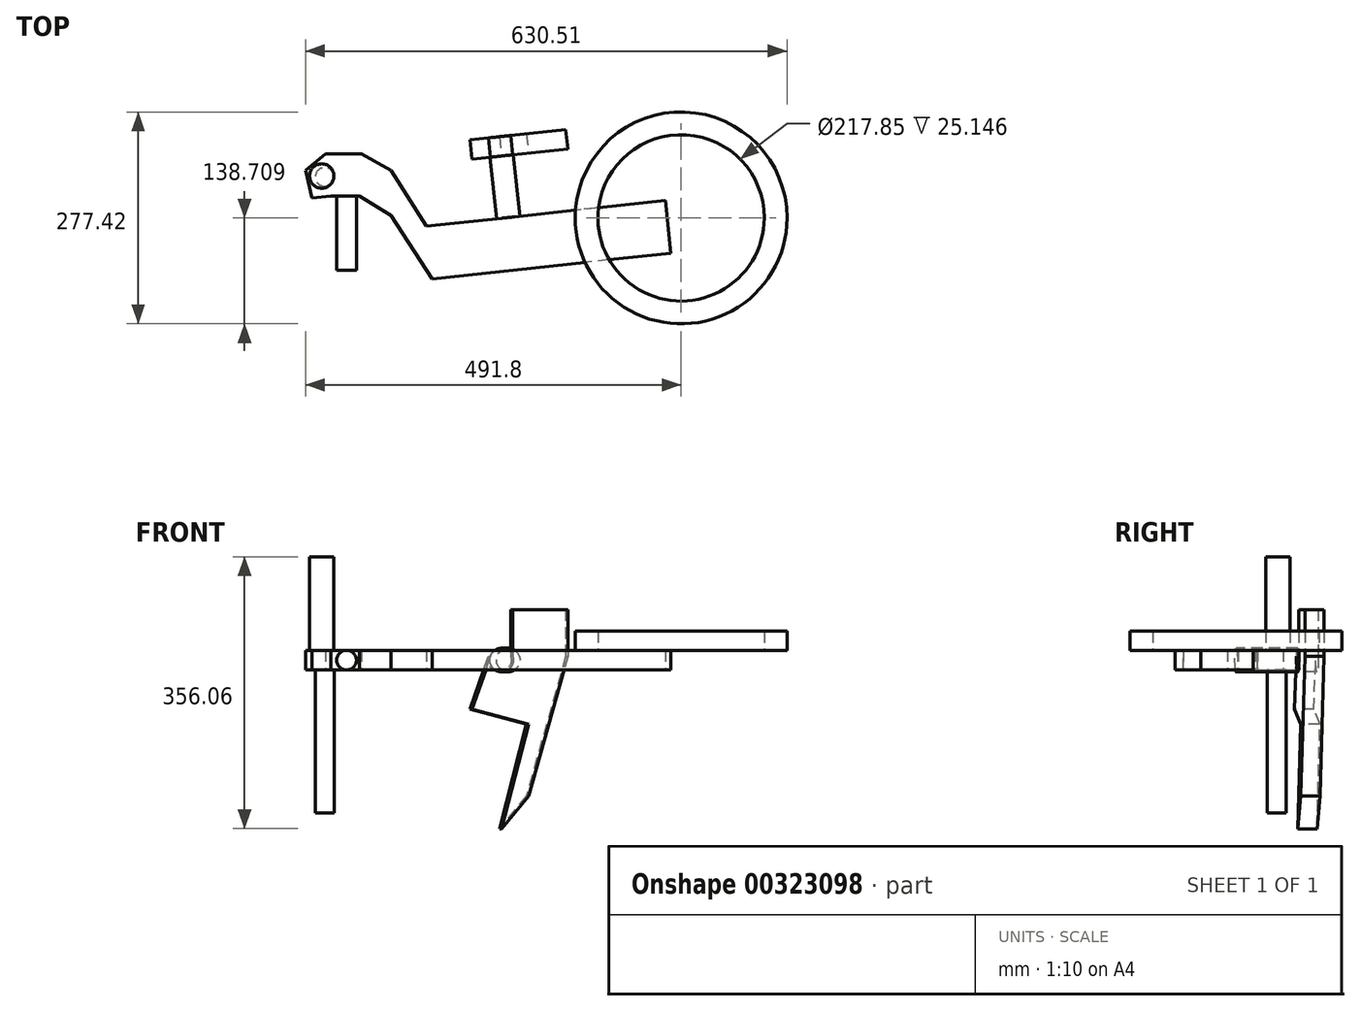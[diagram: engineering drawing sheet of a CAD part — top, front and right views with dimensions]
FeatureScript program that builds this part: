
annotation { "Feature Type Name" : "Feature", "Feature Type Description" : "" }
export const myFeature = defineFeature(function(context is Context, id is Id, definition is map)
    precondition{}
    {
        {
            var Q0;
            Q0=qCreatedBy(makeId("Top.planeOp"),FACE);
            var sketch = newSketch(context, id + "F0", { "sketchPlane" : qUnion([Q0])});
            skLineSegment(sketch, "E0", {"start": v(-102.74, -51.35) * mm, "end": v(-12.48, -51.35) * mm});
            skLineSegment(sketch, "E1", {"start": v(-12.48, -51.35) * mm, "end": v(-6.99, 17.41) * mm});
            skLineSegment(sketch, "E2", {"start": v(-6.99, 17.41) * mm, "end": v(-110.15, 17.41) * mm});
            skLineSegment(sketch, "E3", {"start": v(-110.15, 17.41) * mm, "end": v(-102.74, -51.35) * mm});
            skLineSegment(sketch, "E4", {"start": v(-110.15, 17.41) * mm, "end": v(-156.43, 90.48) * mm});
            skLineSegment(sketch, "E5", {"start": v(-156.43, 90.48) * mm, "end": v(-195.3, 112.17) * mm});
            skLineSegment(sketch, "E6", {"start": v(-195.3, 112.17) * mm, "end": v(-242.66, 112.17) * mm});
            skLineSegment(sketch, "E7", {"start": v(-242.66, 112.17) * mm, "end": v(-268.47, 90.48) * mm});
            skLineSegment(sketch, "E8", {"start": v(-102.74, -51.35) * mm, "end": v(-156.7, 31.5) * mm});
            skLineSegment(sketch, "E9", {"start": v(-156.7, 31.5) * mm, "end": v(-197.7, 56.85) * mm});
            skLineSegment(sketch, "E10", {"start": v(-197.7, 56.85) * mm, "end": v(-235.64, 56.85) * mm});
            skLineSegment(sketch, "E11", {"start": v(-235.64, 56.85) * mm, "end": v(-260.1, 54.22) * mm});
            skLineSegment(sketch, "E12", {"start": v(-260.1, 54.22) * mm, "end": v(-268.47, 90.48) * mm});
            skCircle(sketch, "E13", {"center": v(-247.32, 83.36) * mm, "radius": 15.97 * mm});
            skSolve(sketch);
        }
        {
            var Q0;
            Q0=makeQuery(id+"F0.imprint","IMPRINT",FACE,{"disambiguationData":[TD([[makeQuery(id+"F0.imprint","IMPRINT",EDGE,{"derivedFrom":sQuery(id+"F0.wireOp",EDGE,"E13")}),1.0]])]});
            var Q1;
            Q1=makeQuery(id+"F0.imprint","IMPRINT",FACE,{"disambiguationData":[TD([[makeQuery(id+"F0.imprint","IMPRINT",EDGE,{"derivedFrom":sQuery(id+"F0.wireOp",EDGE,"E3")}),-1.0]])]});
            extrude(context, id + "F1", {"entities" : qUnion([Q0, Q1]), "depth" : 21.34 * mm});
        }
        {
            var Q0;
            Q0=makeQuery(id+"F0.imprint","IMPRINT",FACE,{"disambiguationData":[TD([[makeQuery(id+"F0.imprint","IMPRINT",EDGE,{"derivedFrom":sQuery(id+"F0.wireOp",EDGE,"E13")}),1.0]])]});
            extrude(context, id + "F2", {"entities" : qUnion([Q0]), "operationType" : NewBodyOperationType.ADD, "depth" : 147.83 * mm});
        }
        {
            var Q0;
            Q0=makeQuery(id+"F1.opExtrude","CAP_FACE",FACE,{"disambiguationData":[OSD([sQuery(id+"F0.wireOp",EDGE,"E3"),sQuery(id+"F0.wireOp",EDGE,"E4"),sQuery(id+"F0.wireOp",EDGE,"E5"),sQuery(id+"F0.wireOp",EDGE,"E6"),sQuery(id+"F0.wireOp",EDGE,"E7"),sQuery(id+"F0.wireOp",EDGE,"E8"),sQuery(id+"F0.wireOp",EDGE,"E9"),sQuery(id+"F0.wireOp",EDGE,"E10"),sQuery(id+"F0.wireOp",EDGE,"E11"),sQuery(id+"F0.wireOp",EDGE,"E12")])],"isStart":true});
            var sketch = newSketch(context, id + "F3", { "sketchPlane" : qUnion([Q0])});
            skCircle(sketch, "E14", {"center": v(-243.35, -82.1) * mm, "radius": 12.33 * mm});
            skSolve(sketch);
        }
        {
            var Q0;
            Q0 = qSketchRegion(id + "F3", true);
            extrude(context, id + "F4", {"entities" : qUnion([Q0]), "operationType" : NewBodyOperationType.ADD, "depth" : 187.7 * mm});
        }
        {
            var Q0;
            Q0=makeQuery(id+"F0.imprint","IMPRINT",FACE,{"disambiguationData":[TD([[makeQuery(id+"F0.imprint","IMPRINT",EDGE,{"derivedFrom":sQuery(id+"F0.wireOp",EDGE,"E3")}),-1.0]])]});
            extrude(context, id + "F5", {"entities" : qUnion([Q0]), "operationType" : NewBodyOperationType.ADD, "depth" : 25.4 * mm});
        }
        {
            var Q0;
            {var subQ0=sQuery(id+"F0.wireOp",EDGE,"E3");Q0=makeQuery(id+"F5.boolean.opBoolean","MERGE",FACE,{"derivedFrom":[makeQuery(id+"F1.opExtrude","SWEPT_FACE",FACE,{"disambiguationData":[OSD([subQ0])]}),makeQuery(id+"F5.opExtrude","SWEPT_FACE",FACE,{"disambiguationData":[OSD([subQ0])]})]});}
            var sketch = newSketch(context, id + "F6", { "sketchPlane" : qUnion([Q0])});
            skLineSegment(sketch, "E15.bottom", {"start": v(-40.05, 25.4) * mm, "end": v(29.12, 25.4) * mm});
            skLineSegment(sketch, "E15.top", {"start": v(-40.05, 0) * mm, "end": v(29.12, 0) * mm});
            skLineSegment(sketch, "E15.left", {"start": v(-40.05, 25.4) * mm, "end": v(-40.05, 0) * mm});
            skLineSegment(sketch, "E15.right", {"start": v(29.12, 25.4) * mm, "end": v(29.12, 0) * mm});
            skSolve(sketch);
        }
        {
            var Q0;
            Q0 = qSketchRegion(id + "F6", true);
            extrude(context, id + "F7", {"entities" : qUnion([Q0]), "operationType" : NewBodyOperationType.ADD, "depth" : 314.45 * mm});
        }
        {
            var Q0;
            Q0=makeQuery(id+"F7.boolean.opBoolean","MERGE",FACE,{"derivedFrom":[makeQuery(id+"F5.opExtrude","CAP_FACE",FACE,{"disambiguationData":[OSD([sQuery(id+"F0.wireOp",EDGE,"E3"),sQuery(id+"F0.wireOp",EDGE,"E4"),sQuery(id+"F0.wireOp",EDGE,"E5"),sQuery(id+"F0.wireOp",EDGE,"E6"),sQuery(id+"F0.wireOp",EDGE,"E7"),sQuery(id+"F0.wireOp",EDGE,"E8"),sQuery(id+"F0.wireOp",EDGE,"E9"),sQuery(id+"F0.wireOp",EDGE,"E10"),sQuery(id+"F0.wireOp",EDGE,"E11"),sQuery(id+"F0.wireOp",EDGE,"E12"),sQuery(id+"F0.wireOp",EDGE,"E13")])],"isStart":false}),makeQuery(id+"F7.opExtrude","SWEPT_FACE",FACE,{"disambiguationData":[OSD([sQuery(id+"F6.wireOp",EDGE,"E15.bottom")])]})]});
            var sketch = newSketch(context, id + "F8", { "sketchPlane" : qUnion([Q0])});
            skCircle(sketch, "E16", {"center": v(223.33, 28.47) * mm, "radius": 108.92 * mm});
            skCircle(sketch, "E17", {"center": v(223.33, 28.47) * mm, "radius": 138.7 * mm});
            skSolve(sketch);
        }
        {
            var Q0;
            Q0 = qSketchRegion(id + "F8", true);
            extrude(context, id + "F9", {"entities" : qUnion([Q0]), "operationType" : NewBodyOperationType.ADD, "depth" : 25.15 * mm});
        }
        {
            var Q0;
            Q0=makeQuery(id+"F7.opExtrude","SWEPT_FACE",FACE,{"disambiguationData":[OSD([sQuery(id+"F6.wireOp",EDGE,"E15.right")])]});
            var sketch = newSketch(context, id + "F10", { "sketchPlane" : qUnion([Q0])});
            skCircle(sketch, "E18", {"center": v(0, 12.6) * mm, "radius": 15.44 * mm});
            skSolve(sketch);
        }
        {
            var Q0;
            Q0 = qSketchRegion(id + "F10", true);
            extrude(context, id + "F11", {"entities" : qUnion([Q0]), "operationType" : NewBodyOperationType.ADD, "depth" : 81.03 * mm});
        }
        {
            var Q0;
            Q0=makeQuery(id+"F11.opExtrude","CAP_FACE",FACE,{"disambiguationData":[OSD([sQuery(id+"F10.wireOp",EDGE,"E18")])],"isStart":false});
            var sketch = newSketch(context, id + "F12", { "sketchPlane" : qUnion([Q0])});
            skLineSegment(sketch, "E19", {"start": v(-14.67, 17.43) * mm, "end": v(-87.25, 17.43) * mm});
            skLineSegment(sketch, "E20", {"start": v(-87.25, 17.43) * mm, "end": v(-35.49, -165.41) * mm});
            skLineSegment(sketch, "E21", {"start": v(-35.49, -165.41) * mm, "end": v(0, -208.23) * mm});
            skLineSegment(sketch, "E22", {"start": v(0, -208.23) * mm, "end": v(-35.49, -71.15) * mm});
            skLineSegment(sketch, "E23", {"start": v(-35.49, -71.15) * mm, "end": v(38.96, -51.88) * mm});
            skLineSegment(sketch, "E24", {"start": v(38.96, -51.88) * mm, "end": v(14.58, 17.7) * mm});
            skSolve(sketch);
        }
        {
            var Q0;
            Q0 = qSketchRegion(id + "F12", true);
            var Q1;
            {var subQ0=sQuery(id+"F12.wireOp",EDGE,"E19");Q1=makeQuery(id+"F12.imprint","IMPRINT",FACE,{"disambiguationData":[TD([[makeQuery(id+"F12.imprint","IMPRINT",EDGE,{"derivedFrom":subQ0}),1.0]])]});}
            extrude(context, id + "F13", {"entities" : qUnion([Q0, Q1]), "depth" : 25.4 * mm});
        }
        {
            var Q0;
            Q0=makeQuery(id+"F13.opExtrude","SWEPT_FACE",FACE,{"disambiguationData":[OSD([sQuery(id+"F12.wireOp",EDGE,"E19")])]});
            extrude(context, id + "F14", {"entities" : qUnion([Q0]), "operationType" : NewBodyOperationType.ADD, "depth" : 61.2 * mm});
        }
        {
            var Q0;
            {var subQ0=sQuery(id+"F0.wireOp",EDGE,"E10");Q0=makeQuery(id+"F5.boolean.opBoolean","MERGE",FACE,{"derivedFrom":[makeQuery(id+"F1.opExtrude","SWEPT_FACE",FACE,{"disambiguationData":[OSD([subQ0])]}),makeQuery(id+"F5.opExtrude","SWEPT_FACE",FACE,{"disambiguationData":[OSD([subQ0])]})]});}
            var sketch = newSketch(context, id + "F15", { "sketchPlane" : qUnion([Q0])});
            skCircle(sketch, "E25", {"center": v(-214.8, 12.44) * mm, "radius": 12.96 * mm});
            skSolve(sketch);
        }
        {
            var Q0;
            Q0 = qSketchRegion(id + "F15", true);
            extrude(context, id + "F16", {"entities" : qUnion([Q0]), "operationType" : NewBodyOperationType.ADD, "depth" : 97.03 * mm});
        }
    });
